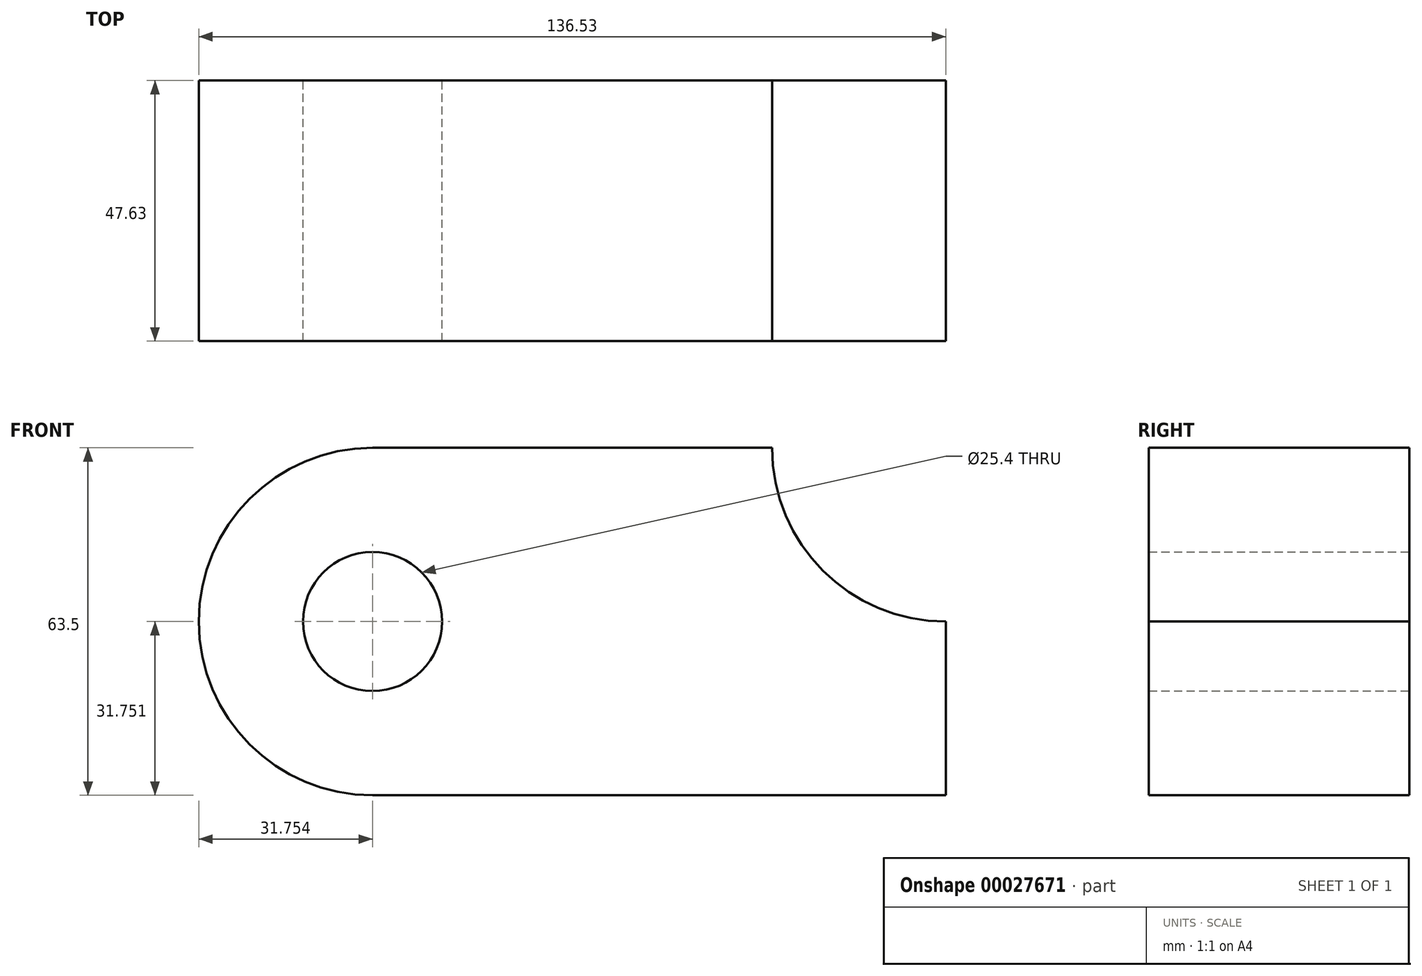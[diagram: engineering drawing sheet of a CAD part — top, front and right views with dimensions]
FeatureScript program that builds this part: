
annotation { "Feature Type Name" : "Feature", "Feature Type Description" : "" }
export const myFeature = defineFeature(function(context is Context, id is Id, definition is map)
    precondition{}
    {
        {
            var Q0;
            Q0=qCreatedBy(makeId("Front.planeOp"),FACE);
            var sketch = newSketch(context, id + "F0", { "sketchPlane" : qUnion([Q0])});
            skArc(sketch, "E0", {"start": v(-13, 32.91) * mm, "mid": v(-44.75, 1.16) * mm, "end": v(-13, -30.59) * mm});
            skLineSegment(sketch, "E1", {"start": v(-13, 32.91) * mm, "end": v(60.03, 32.91) * mm});
            skLineSegment(sketch, "E2", {"start": v(-13, -30.59) * mm, "end": v(91.78, -30.59) * mm});
            skCircle(sketch, "E3", {"center": v(-13, 1.16) * mm, "radius": 12.7 * mm});
            skLineSegment(sketch, "E4", {"start": v(91.78, -30.59) * mm, "end": v(91.78, 1.16) * mm});
            skArc(sketch, "E5", {"start": v(60.03, 32.91) * mm, "mid": v(69.33, 10.46) * mm, "end": v(91.78, 1.16) * mm});
            skSolve(sketch);
        }
        {
            var Q0;
            Q0 = qSketchRegion(id + "F0", true);
            extrude(context, id + "F1", {"entities" : qUnion([Q0]), "depth" : 47.62 * mm});
        }
    });
